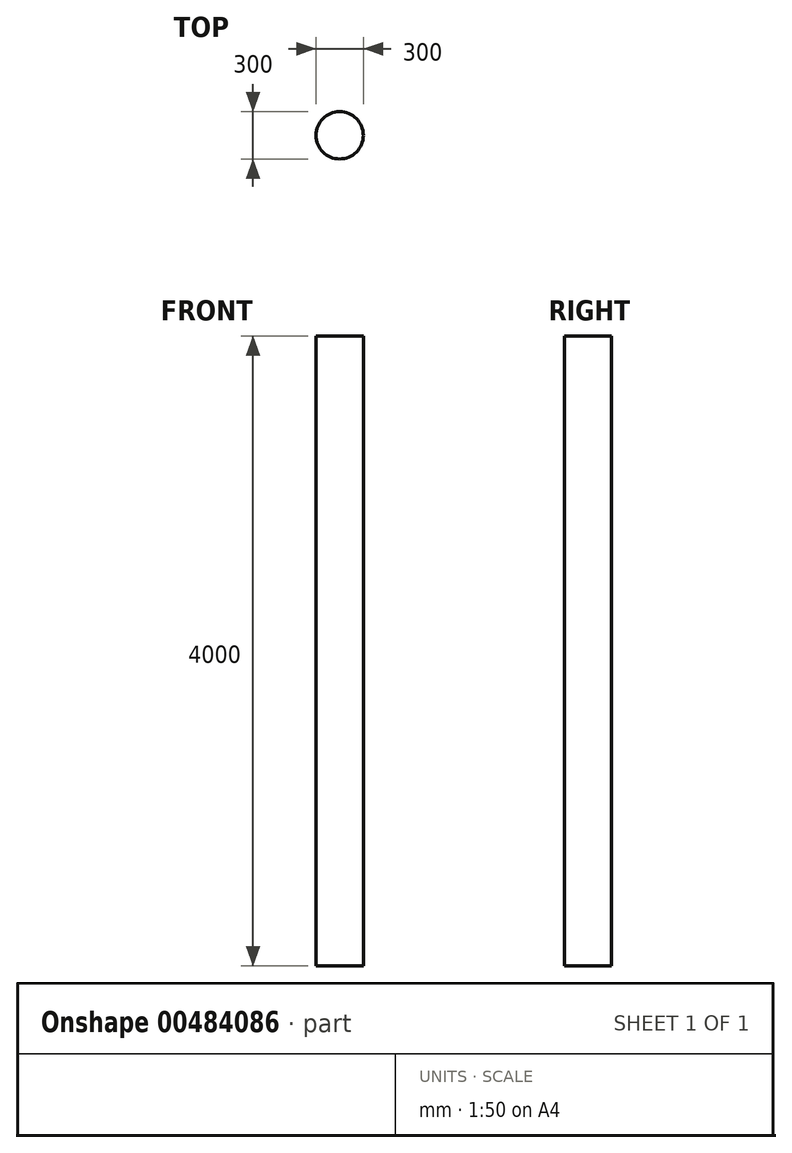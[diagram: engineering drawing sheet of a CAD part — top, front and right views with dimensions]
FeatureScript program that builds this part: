
annotation { "Feature Type Name" : "Feature", "Feature Type Description" : "" }
export const myFeature = defineFeature(function(context is Context, id is Id, definition is map)
    precondition{}
    {
        {
            var Q0;
            Q0=qCreatedBy(makeId("Top.planeOp"),FACE);
            var sketch = newSketch(context, id + "F0", { "sketchPlane" : qUnion([Q0])});
            skCircle(sketch, "E0", {"center": v(0, 0) * mm, "radius": 150 * mm});
            skSolve(sketch);
        }
        {
            var Q0;
            Q0 = qSketchRegion(id + "F0", true);
            extrude(context, id + "F1", {"entities" : qUnion([Q0]), "depth" : 4000 * mm});
        }
    });
